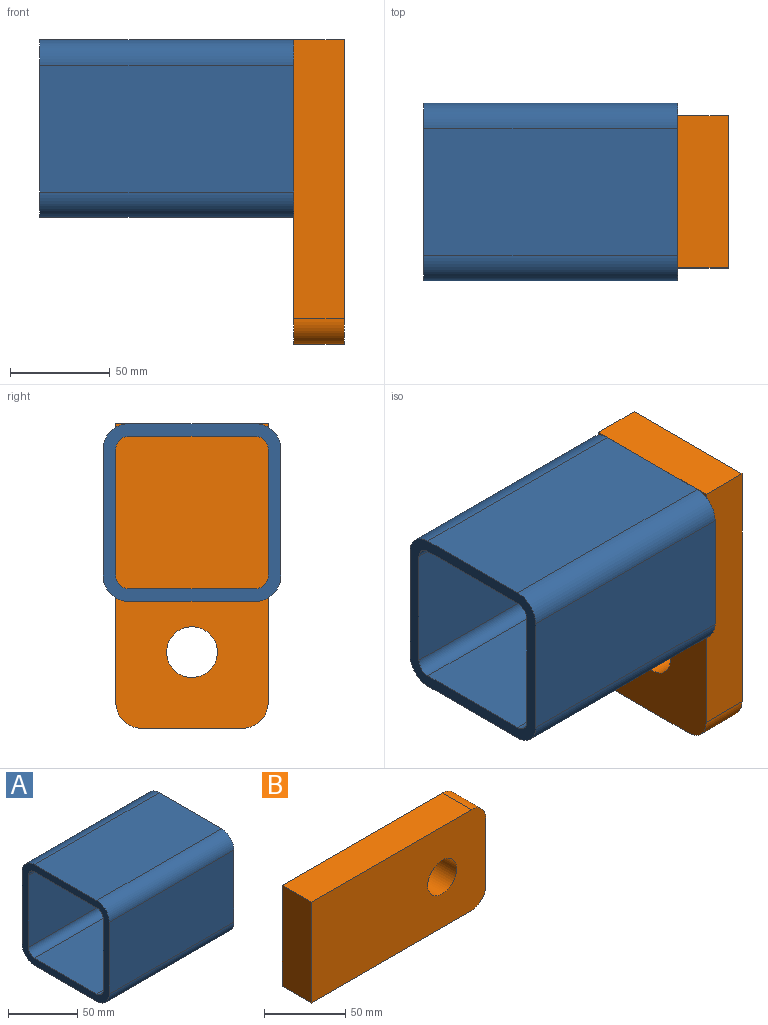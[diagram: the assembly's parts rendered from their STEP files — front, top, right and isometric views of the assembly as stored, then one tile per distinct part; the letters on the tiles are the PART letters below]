
ASSEMBLY  parts=2 mates=1
PART A: 18 faces, bbox 127x88.9x88.9 mm
  f0: plane 127x63.5mm, normal (0,0,1), area 8064.5mm2, adj f1,f7,f8,f9
  f1: cylinder r=12.7mm len=127mm, axis (-1,0,0), area 2533.5mm2, adj f0,f2,f8,f9
  f2: plane 127x63.5mm, normal (0,1,0), area 8064.5mm2, adj f1,f3,f8,f9
  f3: cylinder r=12.7mm len=127mm, axis (-1,0,0), area 2533.5mm2, adj f2,f4,f8,f9
  f4: plane 127x63.5mm, normal (0,0,-1), area 8064.5mm2, adj f3,f5,f8,f9
  f5: cylinder r=12.7mm len=127mm, axis (-1,0,0), area 2533.5mm2, adj f4,f6,f8,f9
  f6: plane 127x63.5mm, normal (0,-1,0), area 8064.5mm2, adj f5,f7,f8,f9
  f7: cylinder r=12.7mm len=127mm, axis (-1,0,0), area 2533.5mm2, adj f0,f6,f8,f9
  f8: plane 88.9x88.9mm, normal (1,0,0), area 1992.9mm2, adj f0,f1,f2,f3,f4,f5,f6,f7
  f9: plane 88.9x88.9mm, normal (-1,0,0), area 1992.9mm2, adj f0,f1,f2,f3,f4,f5,f6,f7
  f10: cylinder r=6.35mm len=127mm, axis (-1,0,0), area 1266.8mm2, adj f8,f9,f11,f17
  f11: plane 127x63.5mm, normal (0,-1,0), area 8064.5mm2, adj f8,f9,f10,f12
  f12: cylinder r=6.35mm len=127mm, axis (-1,0,0), area 1266.8mm2, adj f8,f9,f11,f13
  f13: plane 127x63.5mm, normal (0,0,-1), area 8064.5mm2, adj f8,f9,f12,f14
  f14: cylinder r=6.35mm len=127mm, axis (-1,0,0), area 1266.8mm2, adj f8,f9,f13,f15
  f15: plane 127x63.5mm, normal (0,1,0), area 8064.5mm2, adj f8,f9,f14,f16
  f16: cylinder r=6.35mm len=127mm, axis (-1,0,0), area 1266.8mm2, adj f8,f9,f15,f17
  f17: plane 127x63.5mm, normal (0,0,1), area 8064.5mm2, adj f8,f9,f10,f16
PART B: 9 faces, bbox 152.4x25.4x76.2 mm
  f0: plane 139.7x25.4mm, normal (0,0,1), area 3548.4mm2, adj f1,f5,f7,f8
  f1: plane 76.2x25.4mm, normal (-1,0,0), area 1935.5mm2, adj f0,f2,f7,f8
  f2: plane 139.7x25.4mm, normal (0,0,-1), area 3548.4mm2, adj f1,f3,f7,f8
  f3: cylinder r=12.7mm len=25.4mm, axis (0,1,0), area 506.7mm2, adj f2,f4,f7,f8
  f4: plane 50.8x25.4mm, normal (1,0,0), area 1290.3mm2, adj f3,f5,f7,f8
  f5: cylinder r=12.7mm len=25.4mm, axis (0,1,0), area 506.7mm2, adj f0,f4,f7,f8
  f6: cylinder r=12.7mm len=25.4mm, axis (0,1,0), area 2026.8mm2, adj f7,f8
  f7: plane 152.4x76.2mm, normal (0,-1,0), area 11036.9mm2, adj f0,f1,f2,f3,f4,f5,f6
  f8: plane 152.4x76.2mm, normal (0,1,0), area 11036.9mm2, adj f0,f1,f2,f3,f4,f5,f6
PLACE A t=(122.33,61.75,41.68)mm
PLACE B rot(axis=(0.58,0.58,-0.58),120deg) t=(147.73,61.75,9.93)mm
MATE fastened B.f7 <-> A.f8  axis (-1,0,0) through (122.33,61.75,86.13)mm
